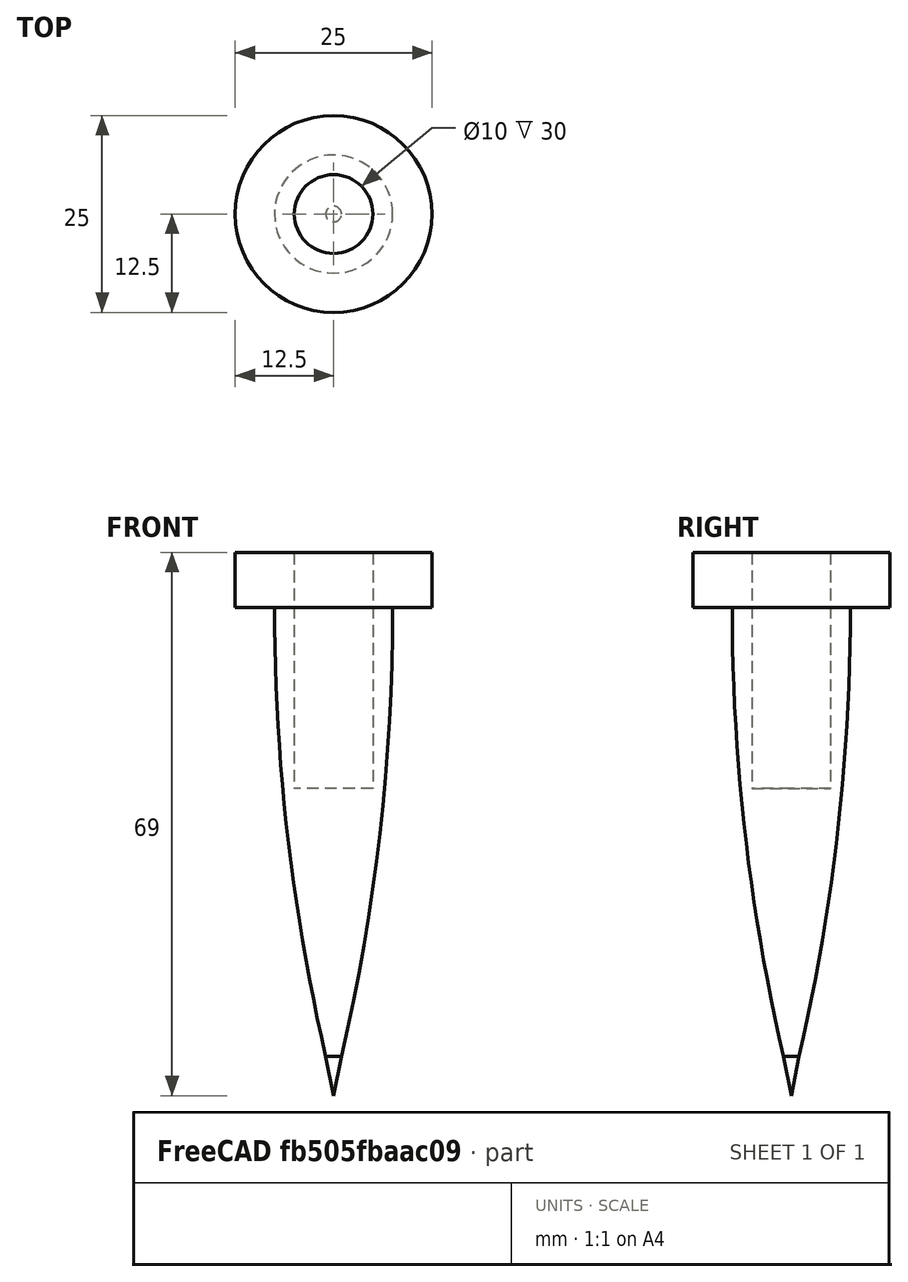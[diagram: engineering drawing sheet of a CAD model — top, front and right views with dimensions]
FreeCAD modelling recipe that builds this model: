
FCSTD DOCUMENT  (FreeCAD 0.18.4R)
Label: part16
License: All rights reserved
LicenseURL: http://en.wikipedia.org/wiki/All_rights_reserved
objects: Sketcher::SketchObject×1, PartDesign::Revolution×1, PartDesign::Body×1
note: 4 computed .brp shape members not serialized (recipe doc carries the construction recipe); baked Part::Feature solids carry a one-line shape summary decoded from their .brp

FEATURE [Sketcher::SketchObject] Sketch
  MapMode = 5
  Placement = pos=(0,0,0) rot=(1,0,0;1.5708rad)
  Support = -> [XZ_Plane]
  sketch-geometry (8):
    g0: LineSegment StartX=7.5 StartY=62 StartZ=0 EndX=12.5 EndY=62 EndZ=0
    g1: LineSegment StartX=12.5 StartY=62 StartZ=0 EndX=12.5 EndY=69 EndZ=0
    g2: LineSegment StartX=12.5 StartY=69 StartZ=0 EndX=5 EndY=69 EndZ=0
    g3: LineSegment StartX=5 StartY=69 StartZ=0 EndX=5 EndY=39 EndZ=0
    g4: LineSegment StartX=5 StartY=39 StartZ=0 EndX=0 EndY=39 EndZ=0
    g5: LineSegment StartX=0 StartY=39 StartZ=0 EndX=0 EndY=0 EndZ=0
    g6: ArcOfCircle CenterX=-245.673 CenterY=62 CenterZ=0 NormalX=0 NormalY=0 NormalZ=1 AngleXU=0 Radius=253.173 StartAngle=6.0561 EndAngle=6.28319
    g7: LineSegment StartX=0 StartY=0 StartZ=0 EndX=1 EndY=5 EndZ=0
  constraints (24):
    c: Horizontal(g0)
    c: Coincident(g0,g1)
    c: Vertical(g1)
    c: Coincident(g1,g2)
    c: Horizontal(g2)
    c: Coincident(g2,g3)
    c: Vertical(g3)
    c: Coincident(g3,g4)
    c: Horizontal(g4)
    c: Coincident(g4,g5)
    c: Vertical(g5)
    c: Coincident(g-1,g5)
    c: DistanceX(g4,g4) = 5
    c: DistanceY(g5,g2) = 69
    c: Coincident(g7,g5)
    c: DistanceX(g5,g7) = 1
    c: DistanceY(g5,g7) = 5
    c: Coincident(g7,g6)
    c: Coincident(g0,g6)
    c: Perpendicular(g6,g0)
    c: DistanceX(g5,g1) = 12.5
    c: DistanceX(g5,g0) = 7.5
    c: DistanceY(g1,g1) = 7
    c: DistanceY(g3,g3) = 30
FEATURE [PartDesign::Revolution] Revolution
  Angle = 360
  Axis = (-3e-16,3e-16,1)
  Base = (0,0,0)
  Placement = pos=(0,0,0) rot=(1,0,0;1.5708rad)
  Profile = -> Sketch
  ReferenceAxis = -> Z_Axis
  Reversed = true
FEATURE [PartDesign::Body] Body
  Group = -> [Sketch,Revolution]
  Origin = -> Origin
  Tip = -> Revolution
